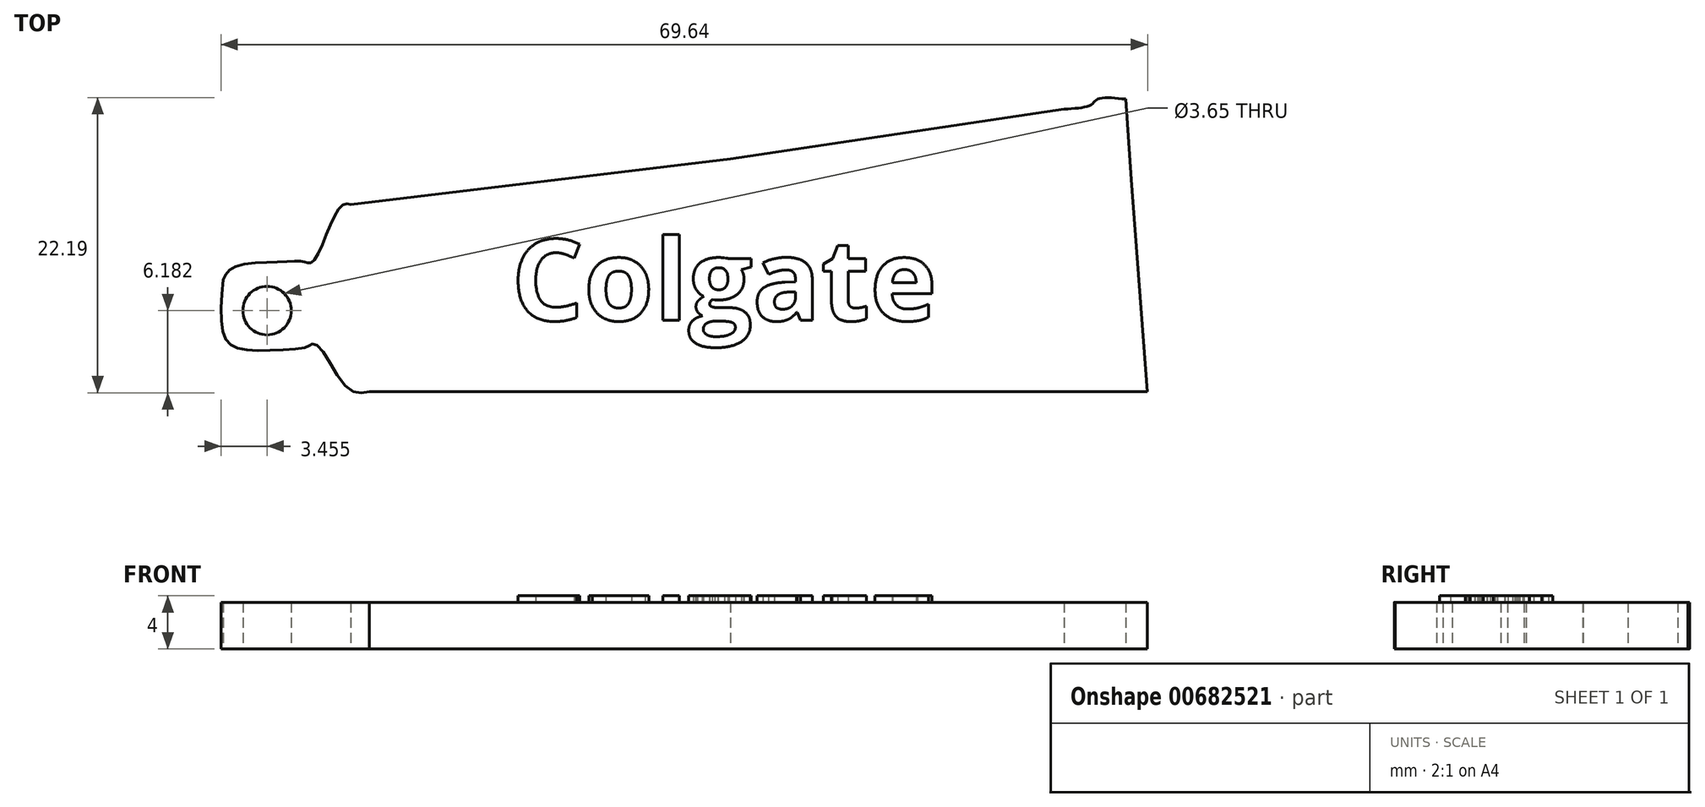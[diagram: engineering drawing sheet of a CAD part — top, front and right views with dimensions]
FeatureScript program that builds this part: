
annotation { "Feature Type Name" : "Feature", "Feature Type Description" : "" }
export const myFeature = defineFeature(function(context is Context, id is Id, definition is map)
    precondition{}
    {
        {
            var Q0;
            Q0=qCreatedBy(makeId("Top.planeOp"),FACE);
            var sketch = newSketch(context, id + "F0", { "sketchPlane" : qUnion([Q0])});
            skLineSegment(sketch, "E0.bottom", {"start": v(-31.12, 15.15) * mm, "end": v(-111.59, 15.15) * mm});
            skLineSegment(sketch, "E0.top", {"start": v(-31.12, 41.31) * mm, "end": v(-111.59, 41.31) * mm});
            skLineSegment(sketch, "E0.left", {"start": v(-31.12, 15.15) * mm, "end": v(-31.12, 41.31) * mm});
            skLineSegment(sketch, "E0.right", {"start": v(-111.59, 15.15) * mm, "end": v(-111.59, 41.31) * mm});
            skFitSpline(sketch, "E1", {"points": [v(-103.81, 25.62) * mm, v(-103.81, 21.65) * mm, v(-102.96, 20.57) * mm, v(-100.3, 20.3) * mm, v(-97.45, 20.57) * mm, v(-97.18, 20.75) * mm, v(-96.64, 20.61) * mm, v(-94.43, 17.46) * mm, v(-92.8, 17.19) * mm], "startDerivative": vector(-2.03, -25.35) * mm, "endDerivative": vector(14.08, 2.3) * mm});
            skLineSegment(sketch, "E2", {"start": v(-92.8, 17.19) * mm, "end": v(-47.84, 17.19) * mm});
            skLineSegment(sketch, "E3", {"start": v(-47.84, 17.19) * mm, "end": v(-37.03, 17.19) * mm});
            skFitSpline(sketch, "E4", {"points": [v(-37.03, 17.19) * mm, v(-36.13, 17.19) * mm, v(-34.32, 17.19) * mm], "startDerivative": vector(2, 0) * mm, "endDerivative": vector(3.34, 0) * mm});
            skLineSegment(sketch, "E5", {"start": v(-34.32, 17.19) * mm, "end": v(-35.54, 33.15) * mm});
            skLineSegment(sketch, "E6", {"start": v(-35.54, 33.15) * mm, "end": v(-35.95, 39.19) * mm});
            skFitSpline(sketch, "E7", {"points": [v(-35.95, 39.19) * mm, v(-38.06, 39.19) * mm, v(-38.57, 38.76) * mm, v(-40.59, 38.44) * mm], "startDerivative": vector(-6.58, 0.71) * mm, "endDerivative": vector(-6.35, -0.35) * mm});
            skLineSegment(sketch, "E8", {"start": v(-40.59, 38.44) * mm, "end": v(-65.66, 34.68) * mm});
            skLineSegment(sketch, "E9", {"start": v(-65.66, 34.68) * mm, "end": v(-94.2, 31.27) * mm});
            skFitSpline(sketch, "E10", {"points": [v(-94.2, 31.27) * mm, v(-94.78, 31.27) * mm, v(-95.86, 29.45) * mm, v(-97.08, 26.96) * mm, v(-97.46, 26.9) * mm, v(-97.84, 27) * mm, v(-99.5, 26.96) * mm, v(-103.06, 26.53) * mm, v(-103.81, 25.62) * mm], "startDerivative": vector(-7.15, 1.86) * mm, "endDerivative": vector(-4.04, -8.96) * mm});
            skLineSegment(sketch, "E11", {"start": v(-100.1, 26.94) * mm, "end": v(-100.1, 26.05) * mm, "construction": true});
            skLineSegment(sketch, "E12", {"start": v(-100.1, 26.05) * mm, "end": v(-100.58, 26.92) * mm, "construction": true});
            skCircle(sketch, "E13", {"center": v(-100.5, 23.3) * mm, "radius": 1.82 * mm});
            skSolve(sketch);
        }
        {
            var Q0;
            Q0=makeQuery(id+"F0.imprint","IMPRINT",FACE,{"disambiguationData":[TD([[makeQuery(id+"F0.imprint","IMPRINT",EDGE,{"derivedFrom":sQuery(id+"F0.wireOp",EDGE,"E1")}),1.0]])]});
            extrude(context, id + "F1", {"entities" : qUnion([Q0]), "depth" : 3.5 * mm, "offsetDistance" : 25 * mm});
        }
        {
            var Q0;
            Q0=makeQuery(id+"F1.opExtrude","CAP_FACE",FACE,{"disambiguationData":[OSD([sQuery(id+"F0.wireOp",EDGE,"E1"),sQuery(id+"F0.wireOp",EDGE,"E2"),sQuery(id+"F0.wireOp",EDGE,"E3"),sQuery(id+"F0.wireOp",EDGE,"E4"),sQuery(id+"F0.wireOp",EDGE,"E5"),sQuery(id+"F0.wireOp",EDGE,"E6"),sQuery(id+"F0.wireOp",EDGE,"E7"),sQuery(id+"F0.wireOp",EDGE,"E8"),sQuery(id+"F0.wireOp",EDGE,"E9"),sQuery(id+"F0.wireOp",EDGE,"E10"),sQuery(id+"F0.wireOp",EDGE,"PeHDtFCv-yPzG-qg6O-CR0w-fcMwPFxgTH5X")])],"isStart":false});
            var sketch = newSketch(context, id + "F2", { "sketchPlane" : qUnion([Q0])});
            skText(sketch, "E14", { "text": "Colgate\n", "fontName": "OpenSans-Bold.ttf"});
            const initialGuessF2  = {"E14": [-0.08213, 0.02255, 1, 0, 0.00613]};
            skSetInitialGuess(sketch, initialGuessF2);
            skSolve(sketch);
        }
        {
            var Q0;
            Q0 = qSketchRegion(id + "F2", true);
            extrude(context, id + "F3", {"entities" : qUnion([Q0]), "operationType" : NewBodyOperationType.ADD, "depth" : 0.5 * mm, "offsetDistance" : 25 * mm});
        }
    });
